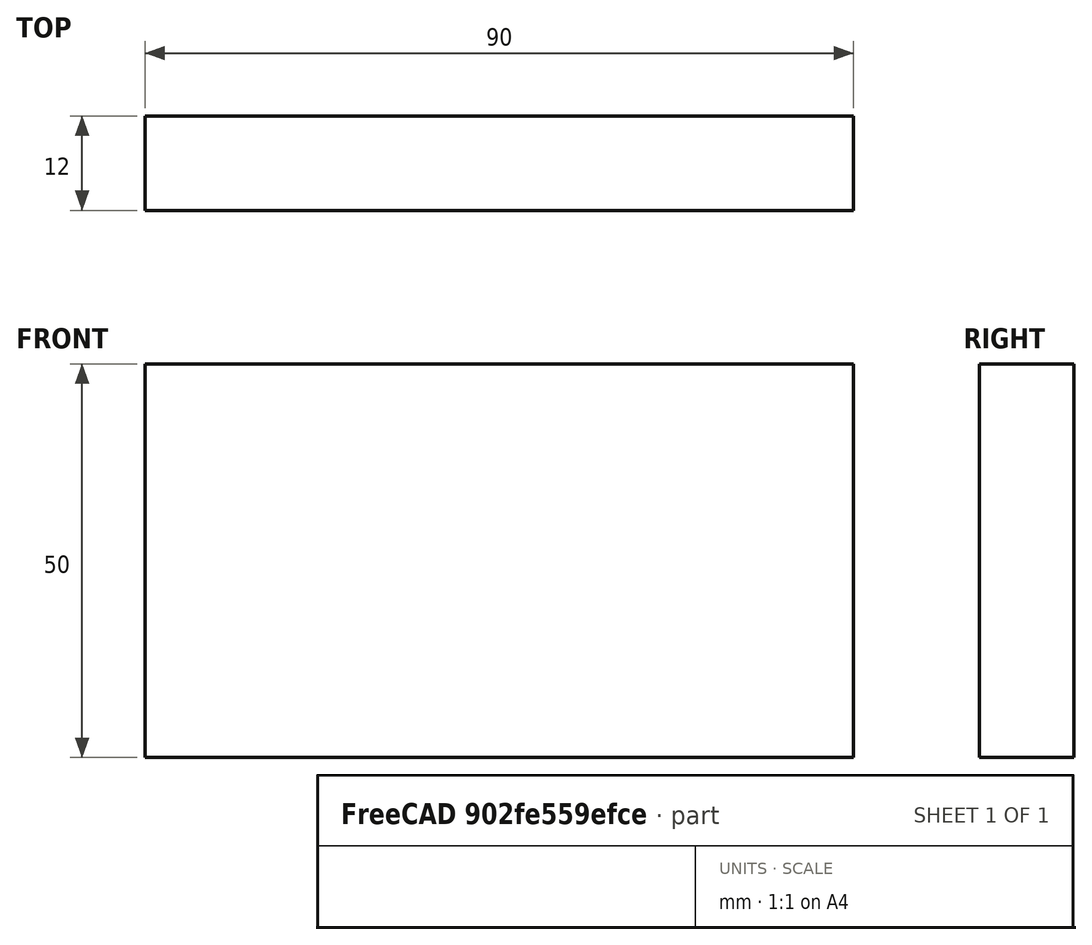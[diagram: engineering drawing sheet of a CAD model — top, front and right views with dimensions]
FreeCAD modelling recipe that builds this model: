
FCSTD DOCUMENT  (FreeCAD 0.15R4671 (Git))
Label: Flat Bar 90x12 EN10058 S235JR
License: All rights reserved
LicenseURL: http://en.wikipedia.org/wiki/All_rights_reserved
objects: Sketcher::SketchObject×1, Part::Extrusion×1
note: 2 computed .brp shape members not serialized (recipe doc carries the construction recipe); baked Part::Feature solids carry a one-line shape summary decoded from their .brp

FEATURE [Sketcher::SketchObject] Sketch
  sketch-geometry (4):
    g0: LineSegment StartX=-45 StartY=-6 StartZ=0 EndX=45 EndY=-6 EndZ=0
    g1: LineSegment StartX=45 StartY=-6 StartZ=0 EndX=45 EndY=6 EndZ=0
    g2: LineSegment StartX=45 StartY=6 StartZ=0 EndX=-45 EndY=6 EndZ=0
    g3: LineSegment StartX=-45 StartY=6 StartZ=0 EndX=-45 EndY=-6 EndZ=0
  constraints (12):
    c: Coincident(g0,g1)
    c: Coincident(g1,g2)
    c: Coincident(g2,g3)
    c: Coincident(g3,g0)
    c: Horizontal(g0)
    c: Horizontal(g2)
    c: Vertical(g1)
    c: Vertical(g3)
    c: Symmetric(g1,g2,g-2)
    c: Symmetric(g0,g1,g-1)
    c: DistanceY(g1) = 12
    c: DistanceX(g0) = 90
FEATURE [Part::Extrusion] Extrude  label="Flat Bar 90x12 EN10058 S235JR"
  Base = -> Sketch
  Dir = (0,0,50)
  Solid = true
